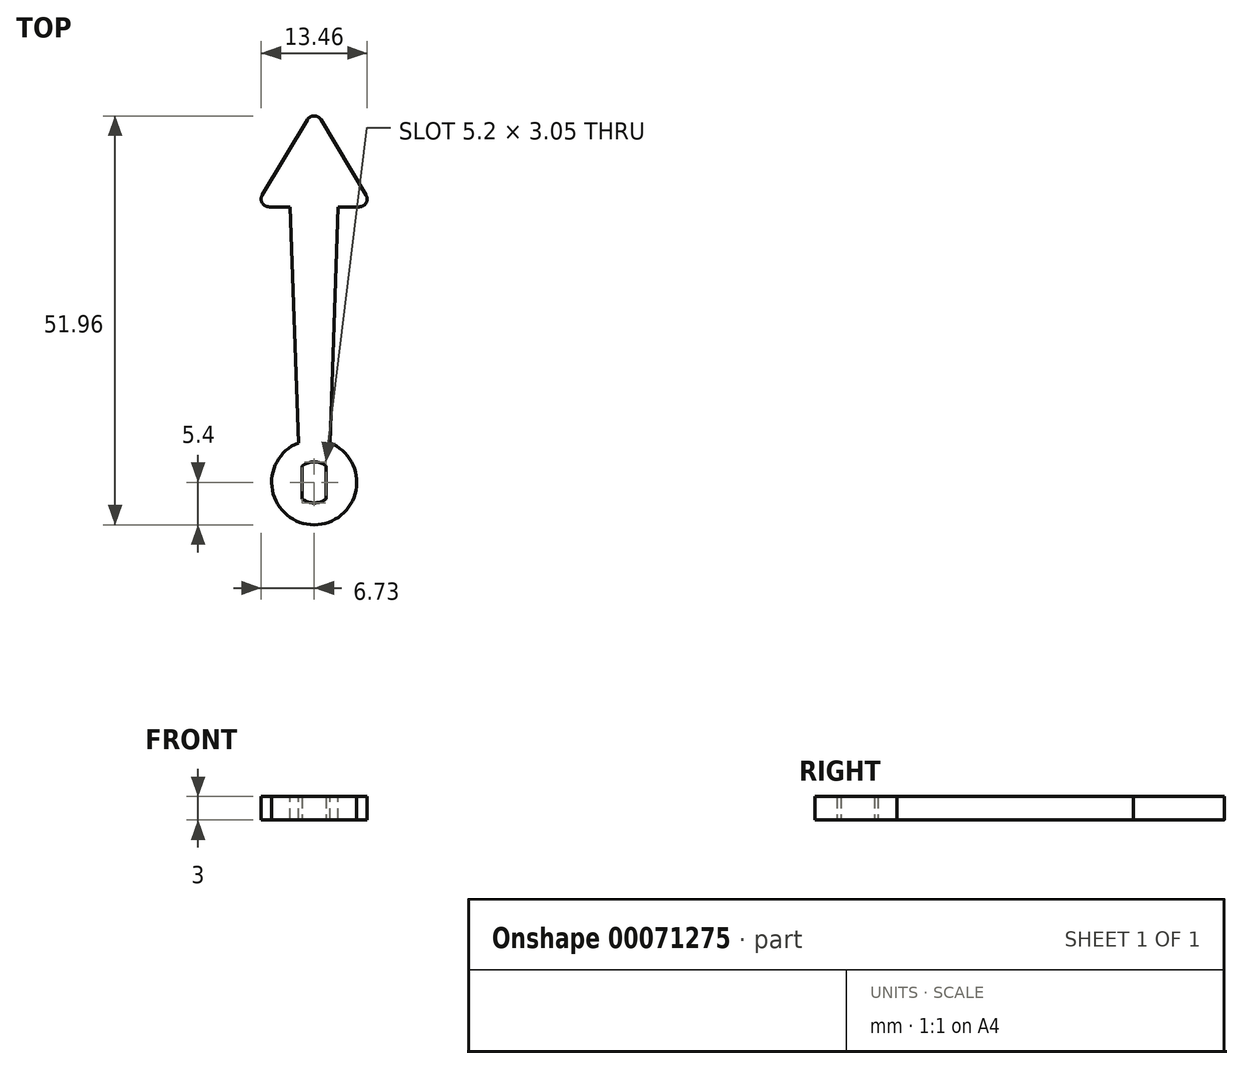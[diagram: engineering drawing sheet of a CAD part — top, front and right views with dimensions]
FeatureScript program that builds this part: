
annotation { "Feature Type Name" : "Feature", "Feature Type Description" : "" }
export const myFeature = defineFeature(function(context is Context, id is Id, definition is map)
    precondition{}
    {
        {
            var Q0;
            Q0=qCreatedBy(makeId("Top.planeOp"),FACE);
            var sketch = newSketch(context, id + "F0", { "sketchPlane" : qUnion([Q0])});
            skCircle(sketch, "E0", {"center": v(0, 0) * mm, "radius": 2.6 * mm});
            skCircle(sketch, "E1", {"center": v(0, 0) * mm, "radius": 5.4 * mm});
            skLineSegment(sketch, "E2", {"start": v(-1.53, 2.1) * mm, "end": v(-1.52, -2.1) * mm});
            skLineSegment(sketch, "E3", {"start": v(1.52, 2.1) * mm, "end": v(1.52, -2.1) * mm});
            skSolve(sketch);
        }
        {
            var Q0;
            Q0=makeQuery(id+"F0.imprint","IMPRINT",FACE,{"disambiguationData":[TD([[makeQuery(id+"F0.imprint","IMPRINT",EDGE,{"derivedFrom":sQuery(id+"F0.wireOp",EDGE,"E1")}),1.0]])]});
            var Q1;
            {var subQ0=sQuery(id+"F0.wireOp",EDGE,"E2");Q1=makeQuery(id+"F0.imprint","IMPRINT",FACE,{"disambiguationData":[TD([[makeQuery(id+"F0.imprint","IMPRINT",EDGE,{"derivedFrom":subQ0}),-1.0]])]});}
            var Q2;
            {var subQ0=sQuery(id+"F0.wireOp",EDGE,"E3");Q2=makeQuery(id+"F0.imprint","IMPRINT",FACE,{"disambiguationData":[TD([[makeQuery(id+"F0.imprint","IMPRINT",EDGE,{"derivedFrom":subQ0}),1.0]])]});}
            extrude(context, id + "F1", {"entities" : qUnion([Q0, Q1, Q2]), "endBound" : BoundingType.SYMMETRIC, "depth" : 3 * mm});
        }
        {
            var Q0;
            Q0=qCreatedBy(makeId("Top.planeOp"),FACE);
            var sketch = newSketch(context, id + "F2", { "sketchPlane" : qUnion([Q0])});
            skLineSegment(sketch, "E4", {"start": v(0, 0) * mm, "end": v(0, 35) * mm, "construction": true});
            skLineSegment(sketch, "E5", {"start": v(2, 5.02) * mm, "end": v(3.05, 35) * mm});
            skLineSegment(sketch, "E6", {"start": v(2, 5.02) * mm, "end": v(0, 5.02) * mm});
            skLineSegment(sketch, "E7", {"start": v(3.05, 35) * mm, "end": v(0, 35) * mm});
            skLineSegment(sketch, "E8.MirrorCS", {"start": v(-2, 5.02) * mm, "end": v(0, 5.02) * mm});
            skLineSegment(sketch, "E9.MirrorCS", {"start": v(-3.05, 35) * mm, "end": v(0, 35) * mm});
            skLineSegment(sketch, "E10.MirrorCS", {"start": v(-2, 5.02) * mm, "end": v(-3.05, 35) * mm});
            skSolve(sketch);
        }
        {
            var Q0;
            Q0=makeQuery(id+"F2.imprint","IMPRINT",FACE,{"disambiguationData":[TD([[makeQuery(id+"F2.imprint","IMPRINT",EDGE,{"derivedFrom":sQuery(id+"F2.wireOp",EDGE,"E5")}),1.0]])]});
            var Q1;
            Q1=makeQuery(id+"F1.opExtrude","CAP_FACE",FACE,{"disambiguationData":[OSD([sQuery(id+"F0.wireOp",EDGE,"E0"),sQuery(id+"F0.wireOp",EDGE,"E1"),sQuery(id+"F0.wireOp",EDGE,"E2"),sQuery(id+"F0.wireOp",EDGE,"E3")])],"isStart":true});
            extrude(context, id + "F3", {"entities" : qUnion([Q0]), "operationType" : NewBodyOperationType.ADD, "endBound" : BoundingType.UP_TO_SURFACE, "oppositeDirection" : true, "endBoundEntityFace" : qUnion([Q1]), "depth" : 25 * mm});
        }
        {
            var Q0;
            Q0=makeQuery(id+"F3.opExtrude","CAP_FACE",FACE,{"disambiguationData":[OSD([sQuery(id+"F2.wireOp",EDGE,"E5"),sQuery(id+"F2.wireOp",EDGE,"E6"),sQuery(id+"F2.wireOp",EDGE,"E7"),sQuery(id+"F2.wireOp",EDGE,"E10.MirrorCS"),sQuery(id+"F2.wireOp",EDGE,"E8.MirrorCS"),sQuery(id+"F2.wireOp",EDGE,"E9.MirrorCS")])],"isStart":true});
            var Q1;
            Q1=makeQuery(id+"F1.opExtrude","CAP_FACE",FACE,{"disambiguationData":[OSD([sQuery(id+"F0.wireOp",EDGE,"E0"),sQuery(id+"F0.wireOp",EDGE,"E1"),sQuery(id+"F0.wireOp",EDGE,"E2"),sQuery(id+"F0.wireOp",EDGE,"E3")])],"isStart":false});
            extrude(context, id + "F4", {"entities" : qUnion([Q0]), "operationType" : NewBodyOperationType.ADD, "endBound" : BoundingType.UP_TO_SURFACE, "endBoundEntityFace" : qUnion([Q1]), "depth" : 25 * mm});
        }
        {
            var Q0;
            Q0=qCreatedBy(makeId("Top.planeOp"),FACE);
            var sketch = newSketch(context, id + "F5", { "sketchPlane" : qUnion([Q0])});
            skLineSegment(sketch, "E11", {"start": v(0, 35) * mm, "end": v(0, 47.5) * mm, "construction": true});
            skLineSegment(sketch, "E12", {"start": v(-7.5, 35) * mm, "end": v(7.5, 35) * mm});
            skLineSegment(sketch, "E13", {"start": v(-7.5, 35) * mm, "end": v(0, 47.5) * mm});
            skLineSegment(sketch, "E14", {"start": v(0, 47.5) * mm, "end": v(7.5, 35) * mm});
            skSolve(sketch);
        }
        {
            var Q0;
            Q0=makeQuery(id+"F5.imprint","IMPRINT",FACE,{"disambiguationData":[TD([[makeQuery(id+"F5.imprint","IMPRINT",EDGE,{"derivedFrom":sQuery(id+"F5.wireOp",EDGE,"E12")}),1.0]])]});
            var Q1;
            Q1=makeQuery(id+"F3.boolean.opBoolean","MERGE",FACE,{"derivedFrom":[makeQuery(id+"F1.opExtrude","CAP_FACE",FACE,{"disambiguationData":[OSD([sQuery(id+"F0.wireOp",EDGE,"E0"),sQuery(id+"F0.wireOp",EDGE,"E1"),sQuery(id+"F0.wireOp",EDGE,"E2"),sQuery(id+"F0.wireOp",EDGE,"E3")])],"isStart":true}),makeQuery(id+"F3.opExtrude","CAP_FACE",FACE,{"disambiguationData":[OSD([sQuery(id+"F2.wireOp",EDGE,"E5"),sQuery(id+"F2.wireOp",EDGE,"E6"),sQuery(id+"F2.wireOp",EDGE,"E7"),sQuery(id+"F2.wireOp",EDGE,"E10.MirrorCS"),sQuery(id+"F2.wireOp",EDGE,"E8.MirrorCS"),sQuery(id+"F2.wireOp",EDGE,"E9.MirrorCS")])],"isStart":false})]});
            extrude(context, id + "F6", {"entities" : qUnion([Q0]), "operationType" : NewBodyOperationType.ADD, "endBound" : BoundingType.UP_TO_SURFACE, "oppositeDirection" : true, "endBoundEntityFace" : qUnion([Q1]), "depth" : 25 * mm});
        }
        {
            var Q0;
            Q0=makeQuery(id+"F6.opExtrude","CAP_FACE",FACE,{"disambiguationData":[OSD([sQuery(id+"F5.wireOp",EDGE,"E12"),sQuery(id+"F5.wireOp",EDGE,"E13"),sQuery(id+"F5.wireOp",EDGE,"E14")])],"isStart":true});
            var Q1;
            Q1=makeQuery(id+"F4.boolean.opBoolean","MERGE",FACE,{"derivedFrom":[makeQuery(id+"F1.opExtrude","CAP_FACE",FACE,{"disambiguationData":[OSD([sQuery(id+"F0.wireOp",EDGE,"E0"),sQuery(id+"F0.wireOp",EDGE,"E1"),sQuery(id+"F0.wireOp",EDGE,"E2"),sQuery(id+"F0.wireOp",EDGE,"E3")])],"isStart":false}),makeQuery(id+"F4.opExtrude","CAP_FACE",FACE,{"disambiguationData":[OSD([sQuery(id+"F2.wireOp",EDGE,"E5"),sQuery(id+"F2.wireOp",EDGE,"E6"),sQuery(id+"F2.wireOp",EDGE,"E7"),sQuery(id+"F2.wireOp",EDGE,"E10.MirrorCS"),sQuery(id+"F2.wireOp",EDGE,"E8.MirrorCS"),sQuery(id+"F2.wireOp",EDGE,"E9.MirrorCS")])],"isStart":false})]});
            extrude(context, id + "F7", {"entities" : qUnion([Q0]), "operationType" : NewBodyOperationType.ADD, "endBound" : BoundingType.UP_TO_SURFACE, "endBoundEntityFace" : qUnion([Q1]), "depth" : 25 * mm});
        }
        {
            var Q0;
            {var subQ0=sQuery(id+"F5.wireOp",EDGE,"E14");var subQ1=sQuery(id+"F5.wireOp",EDGE,"E12");Q0=makeQuery(id+"F7.boolean.opBoolean","MERGE",EDGE,{"derivedFrom":[makeQuery(id+"F6.opExtrude","SWEPT_EDGE",EDGE,{"disambiguationData":[OSD([subQ1,subQ0])]}),makeQuery(id+"F7.opExtrude","SWEPT_EDGE",EDGE,{"disambiguationData":[OSD([subQ1,subQ0])]})]});}
            var Q1;
            {var subQ0=sQuery(id+"F5.wireOp",EDGE,"E14");var subQ1=sQuery(id+"F5.wireOp",EDGE,"E13");Q1=makeQuery(id+"F7.boolean.opBoolean","MERGE",EDGE,{"derivedFrom":[makeQuery(id+"F6.opExtrude","SWEPT_EDGE",EDGE,{"disambiguationData":[OSD([subQ1,subQ0])]}),makeQuery(id+"F7.opExtrude","SWEPT_EDGE",EDGE,{"disambiguationData":[OSD([subQ1,subQ0])]})]});}
            var Q2;
            {var subQ0=sQuery(id+"F5.wireOp",EDGE,"E13");var subQ1=sQuery(id+"F5.wireOp",EDGE,"E12");Q2=makeQuery(id+"F7.boolean.opBoolean","MERGE",EDGE,{"derivedFrom":[makeQuery(id+"F6.opExtrude","SWEPT_EDGE",EDGE,{"disambiguationData":[OSD([subQ1,subQ0])]}),makeQuery(id+"F7.opExtrude","SWEPT_EDGE",EDGE,{"disambiguationData":[OSD([subQ1,subQ0])]})]});}
            fillet(context, id + "F8", {"entities" : qUnion([Q0, Q1, Q2]), "radius" : 1 * mm, "tangentPropagation" : true, "allowEdgeOverflow" : false});
        }
    });
